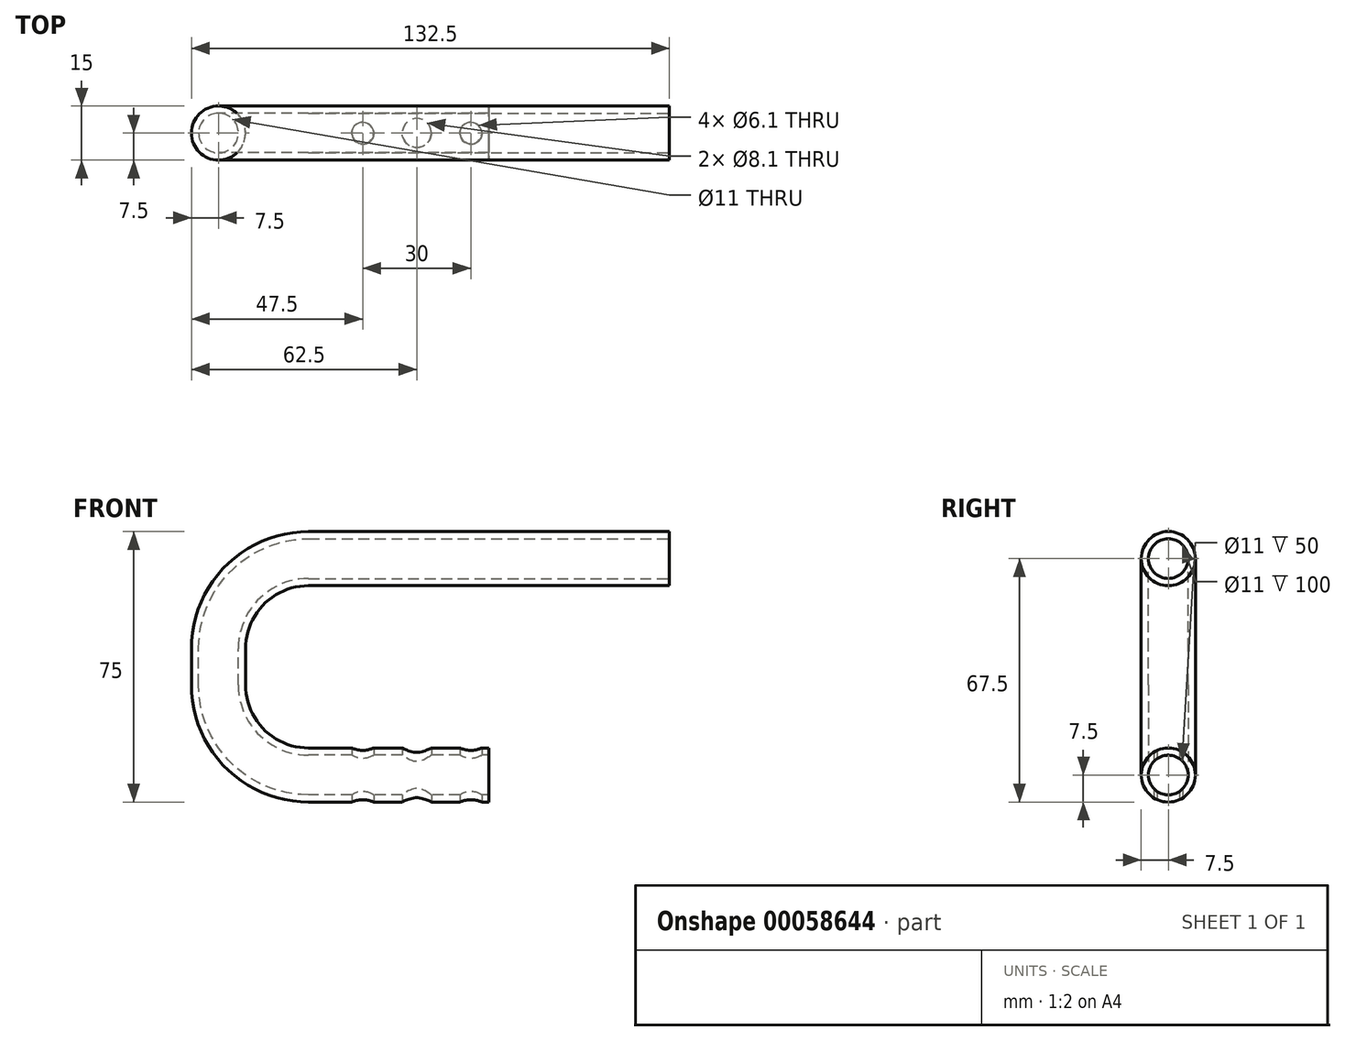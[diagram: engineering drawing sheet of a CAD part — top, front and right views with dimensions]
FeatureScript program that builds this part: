
annotation { "Feature Type Name" : "Feature", "Feature Type Description" : "" }
export const myFeature = defineFeature(function(context is Context, id is Id, definition is map)
    precondition{}
    {
        {
            var Q0;
            Q0=qCreatedBy(makeId("Right.planeOp"),FACE);
            var sketch = newSketch(context, id + "F0", { "sketchPlane" : qUnion([Q0])});
            skCircle(sketch, "E0", {"center": v(0, 0) * mm, "radius": 7.5 * mm});
            skCircle(sketch, "E1", {"center": v(0, 0) * mm, "radius": 5.5 * mm});
            skSolve(sketch);
        }
        {
            var Q0;
            Q0=qCreatedBy(makeId("Front.planeOp"),FACE);
            var sketch = newSketch(context, id + "F1", { "sketchPlane" : qUnion([Q0])});
            skLineSegment(sketch, "E2", {"start": v(0, 0) * mm, "end": v(-50, 0) * mm});
            skLineSegment(sketch, "E3", {"start": v(-75, 25) * mm, "end": v(-75, 35) * mm});
            skLineSegment(sketch, "E4", {"start": v(-50, 60) * mm, "end": v(50, 60) * mm});
            skPoint(sketch, "E5.visualSharp", {"position": v(-75, 0) * mm});
            skArc(sketch, "E5.filletArc", {"start": v(-75, 25) * mm, "mid": v(-67.68, 7.32) * mm, "end": v(-50, 0) * mm});
            skPoint(sketch, "E6.visualSharp", {"position": v(-75, 60) * mm});
            skArc(sketch, "E6.filletArc", {"start": v(-50, 60) * mm, "mid": v(-67.68, 52.68) * mm, "end": v(-75, 35) * mm});
            skSolve(sketch);
        }
        {
            var Q0;
            Q0=makeQuery(id+"F0.imprint","IMPRINT",FACE,{"disambiguationData":[TD([[makeQuery(id+"F0.imprint","IMPRINT",EDGE,{"derivedFrom":sQuery(id+"F0.wireOp",EDGE,"E0")}),1.0]])]});
            var Q1;
            Q1=sQuery(id+"F1.wireOp",EDGE,"E2");
            var Q2;
            Q2=sQuery(id+"F1.wireOp",EDGE,"E5.filletArc");
            var Q3;
            Q3=sQuery(id+"F1.wireOp",EDGE,"E3");
            var Q4;
            Q4=sQuery(id+"F1.wireOp",EDGE,"E6.filletArc");
            var Q5;
            Q5=sQuery(id+"F1.wireOp",EDGE,"E4");
            sweep(context, id + "F2", {"profiles" : qUnion([Q0]), "path" : qUnion([Q1, Q2, Q3, Q4, Q5])});
        }
        {
            var Q0;
            Q0=qCreatedBy(makeId("Top.planeOp"),FACE);
            var sketch = newSketch(context, id + "F3", { "sketchPlane" : qUnion([Q0])});
            skCircle(sketch, "E7", {"center": v(-20, 0) * mm, "radius": 4.05 * mm});
            skCircle(sketch, "E8", {"center": v(-5, 0) * mm, "radius": 3.05 * mm});
            skCircle(sketch, "E9", {"center": v(-35, 0) * mm, "radius": 3.05 * mm});
            skSolve(sketch);
        }
        {
            var Q0;
            Q0=qSketchRegion(id+"F3",true);
            extrude(context, id + "F4", {"entities" : qUnion([Q0]), "endBound" : BoundingType.SYMMETRIC, "depth" : 30 * mm});
        }
        {
            var Q0;
            Q0=makeQuery(id+"F4.opExtrude","SWEPT_BODY",BODY,{"disambiguationData":[OSD([sQuery(id+"F3.wireOp",EDGE,"E9")])]});
            var Q1;
            Q1=makeQuery(id+"F4.opExtrude","SWEPT_BODY",BODY,{"disambiguationData":[OSD([sQuery(id+"F3.wireOp",EDGE,"E7")])]});
            var Q2;
            Q2=makeQuery(id+"F4.opExtrude","SWEPT_BODY",BODY,{"disambiguationData":[OSD([sQuery(id+"F3.wireOp",EDGE,"E8")])]});
            var Q3;
            Q3=makeQuery(id+"F2.opSweep","SWEPT_BODY",BODY,{"disambiguationData":[OSD([sQuery(id+"F0.wireOp",EDGE,"E0"),sQuery(id+"F0.wireOp",EDGE,"E1"),sQuery(id+"F1.wireOp",EDGE,"E4")])]});
            booleanBodies(context, id + "F5", {"operationType" : BooleanOperationType.SUBTRACTION, "tools" : qUnion([Q0, Q1, Q2]), "targets" : qUnion([Q3])});
        }
    });
